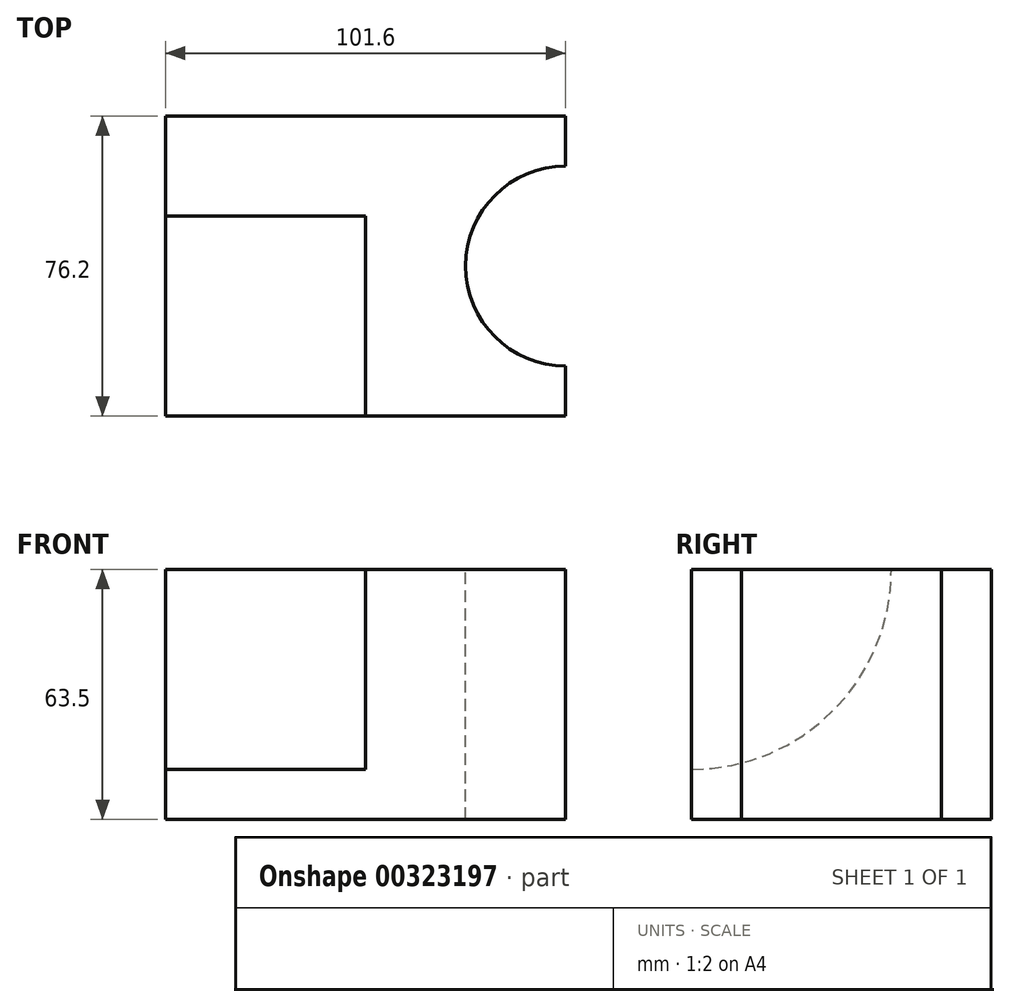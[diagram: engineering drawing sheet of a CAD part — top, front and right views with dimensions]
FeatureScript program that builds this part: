
annotation { "Feature Type Name" : "Feature", "Feature Type Description" : "" }
export const myFeature = defineFeature(function(context is Context, id is Id, definition is map)
    precondition{}
    {
        {
            var Q0;
            Q0=qCreatedBy(makeId("Right.planeOp"),FACE);
            var sketch = newSketch(context, id + "F0", { "sketchPlane" : qUnion([Q0])});
            skLineSegment(sketch, "E0.bottom", {"start": v(-31.89, 16.3) * mm, "end": v(44.31, 16.3) * mm});
            skLineSegment(sketch, "E0.top", {"start": v(-31.89, -47.2) * mm, "end": v(44.31, -47.2) * mm});
            skLineSegment(sketch, "E0.left", {"start": v(-31.89, 16.3) * mm, "end": v(-31.89, -47.2) * mm});
            skLineSegment(sketch, "E0.right", {"start": v(44.31, 16.3) * mm, "end": v(44.31, -47.2) * mm});
            skSolve(sketch);
        }
        {
            var Q0;
            Q0=makeQuery(id+"F0.imprint","IMPRINT",FACE,{"disambiguationData":[TD([[makeQuery(id+"F0.imprint","IMPRINT",EDGE,{"derivedFrom":sQuery(id+"F0.wireOp",EDGE,"E0.bottom")}),-1.0]])]});
            extrude(context, id + "F1", {"entities" : qUnion([Q0]), "oppositeDirection" : true, "depth" : 101.6 * mm});
        }
        {
            var Q0;
            Q0=makeQuery(id+"F1.opExtrude","SWEPT_FACE",FACE,{"disambiguationData":[OSD([sQuery(id+"F0.wireOp",EDGE,"E0.bottom")])]});
            var sketch = newSketch(context, id + "F2", { "sketchPlane" : qUnion([Q0])});
            skArc(sketch, "E1", {"start": v(0, 31.61) * mm, "mid": v(-25.4, 6.21) * mm, "end": v(0, -19.19) * mm});
            skLineSegment(sketch, "E2", {"start": v(0, 31.61) * mm, "end": v(0, -19.19) * mm});
            skSolve(sketch);
        }
        {
            var Q0;
            Q0=makeQuery(id+"F2.imprint","IMPRINT",FACE,{"disambiguationData":[TD([[makeQuery(id+"F2.imprint","IMPRINT",EDGE,{"derivedFrom":sQuery(id+"F2.wireOp",EDGE,"E1")}),1.0]])]});
            extrude(context, id + "F3", {"entities" : qUnion([Q0]), "operationType" : NewBodyOperationType.REMOVE, "oppositeDirection" : true, "depth" : 63.5 * mm});
        }
        {
            var Q0;
            Q0=makeQuery(id+"F1.opExtrude","CAP_FACE",FACE,{"disambiguationData":[OSD([sQuery(id+"F0.wireOp",EDGE,"E0.bottom"),sQuery(id+"F0.wireOp",EDGE,"E0.top"),sQuery(id+"F0.wireOp",EDGE,"E0.left"),sQuery(id+"F0.wireOp",EDGE,"E0.right")])],"isStart":false});
            var sketch = newSketch(context, id + "F4", { "sketchPlane" : qUnion([Q0])});
            skArc(sketch, "E3", {"start": v(-18.91, 16.3) * mm, "mid": v(-4.03, -19.62) * mm, "end": v(31.89, -34.5) * mm});
            skLineSegment(sketch, "E4", {"start": v(-18.91, 16.3) * mm, "end": v(31.89, 16.3) * mm});
            skLineSegment(sketch, "E5", {"start": v(31.89, 16.3) * mm, "end": v(31.89, -34.5) * mm});
            skSolve(sketch);
        }
        {
            var Q0;
            Q0=makeQuery(id+"F4.imprint","IMPRINT",FACE,{"disambiguationData":[TD([[makeQuery(id+"F4.imprint","IMPRINT",EDGE,{"derivedFrom":sQuery(id+"F4.wireOp",EDGE,"E3")}),1.0]])]});
            extrude(context, id + "F5", {"entities" : qUnion([Q0]), "operationType" : NewBodyOperationType.REMOVE, "oppositeDirection" : true, "depth" : 50.8 * mm});
        }
    });
